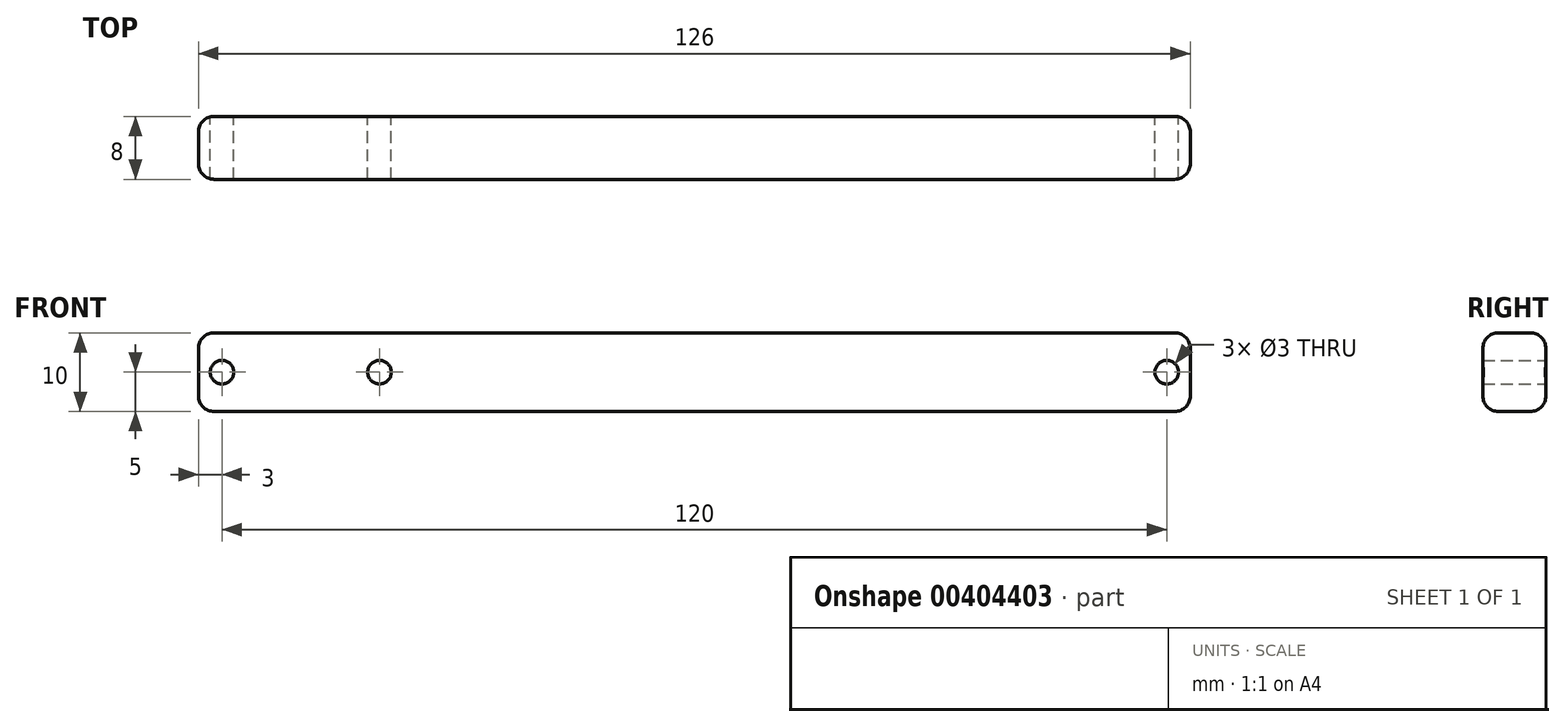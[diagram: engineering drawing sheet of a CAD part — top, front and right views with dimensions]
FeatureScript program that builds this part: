
annotation { "Feature Type Name" : "Feature", "Feature Type Description" : "" }
export const myFeature = defineFeature(function(context is Context, id is Id, definition is map)
    precondition{}
    {
        {
            var Q0;
            Q0=qCreatedBy(makeId("Front.planeOp"),FACE);
            var sketch = newSketch(context, id + "F0", { "sketchPlane" : qUnion([Q0])});
            skLineSegment(sketch, "E0.bottom", {"start": v(-63, 0) * mm, "end": v(63, 0) * mm});
            skLineSegment(sketch, "E0.top", {"start": v(-63, 10) * mm, "end": v(63, 10) * mm});
            skLineSegment(sketch, "E0.left", {"start": v(-63, 0) * mm, "end": v(-63, 10) * mm});
            skLineSegment(sketch, "E0.right", {"start": v(63, 0) * mm, "end": v(63, 10) * mm});
            skCircle(sketch, "E1", {"center": v(60, 5) * mm, "radius": 1.5 * mm});
            skCircle(sketch, "E2.1.0.0", {"center": v(-60, 5) * mm, "radius": 1.5 * mm});
            skLineSegment(sketch, "E2.direction1", {"start": v(60, 5) * mm, "end": v(-60, 5) * mm, "construction": true});
            skCircle(sketch, "E3", {"center": v(-40, 5) * mm, "radius": 1.5 * mm});
            skSolve(sketch);
        }
        {
            var Q0;
            Q0=makeQuery(id+"F0.imprint","IMPRINT",FACE,{"disambiguationData":[TD([[makeQuery(id+"F0.imprint","IMPRINT",EDGE,{"derivedFrom":sQuery(id+"F0.wireOp",EDGE,"E0.bottom")}),1.0]])]});
            var Q1;
            Q1=sQuery(id+"F0.wireOp",EDGE,"E0.top");
            extrude(context, id + "F1", {"entities" : qUnion([Q0]), "surfaceEntities" : qUnion([Q1]), "depth" : 8 * mm});
        }
        {
            var Q0;
            Q0=makeQuery(id+"F1.opExtrude","SWEPT_FACE",FACE,{"disambiguationData":[OSD([sQuery(id+"F0.wireOp",EDGE,"E0.top")])]});
            var Q1;
            Q1=makeQuery(id+"F1.opExtrude","SWEPT_FACE",FACE,{"disambiguationData":[OSD([sQuery(id+"F0.wireOp",EDGE,"E0.right")])]});
            fillet(context, id + "F2", {"entities" : qUnion([Q0, Q1]), "radius" : 2 * mm, "tangentPropagation" : true, "allowEdgeOverflow" : false});
        }
        {
            var Q0;
            Q0=makeQuery(id+"F1.opExtrude","SWEPT_FACE",FACE,{"disambiguationData":[OSD([sQuery(id+"F0.wireOp",EDGE,"E0.left")])]});
            var Q1;
            Q1=makeQuery(id+"F1.opExtrude","SWEPT_FACE",FACE,{"disambiguationData":[OSD([sQuery(id+"F0.wireOp",EDGE,"E0.bottom")])]});
            fillet(context, id + "F3", {"entities" : qUnion([Q0, Q1]), "radius" : 2 * mm, "tangentPropagation" : true, "allowEdgeOverflow" : false});
        }
    });
